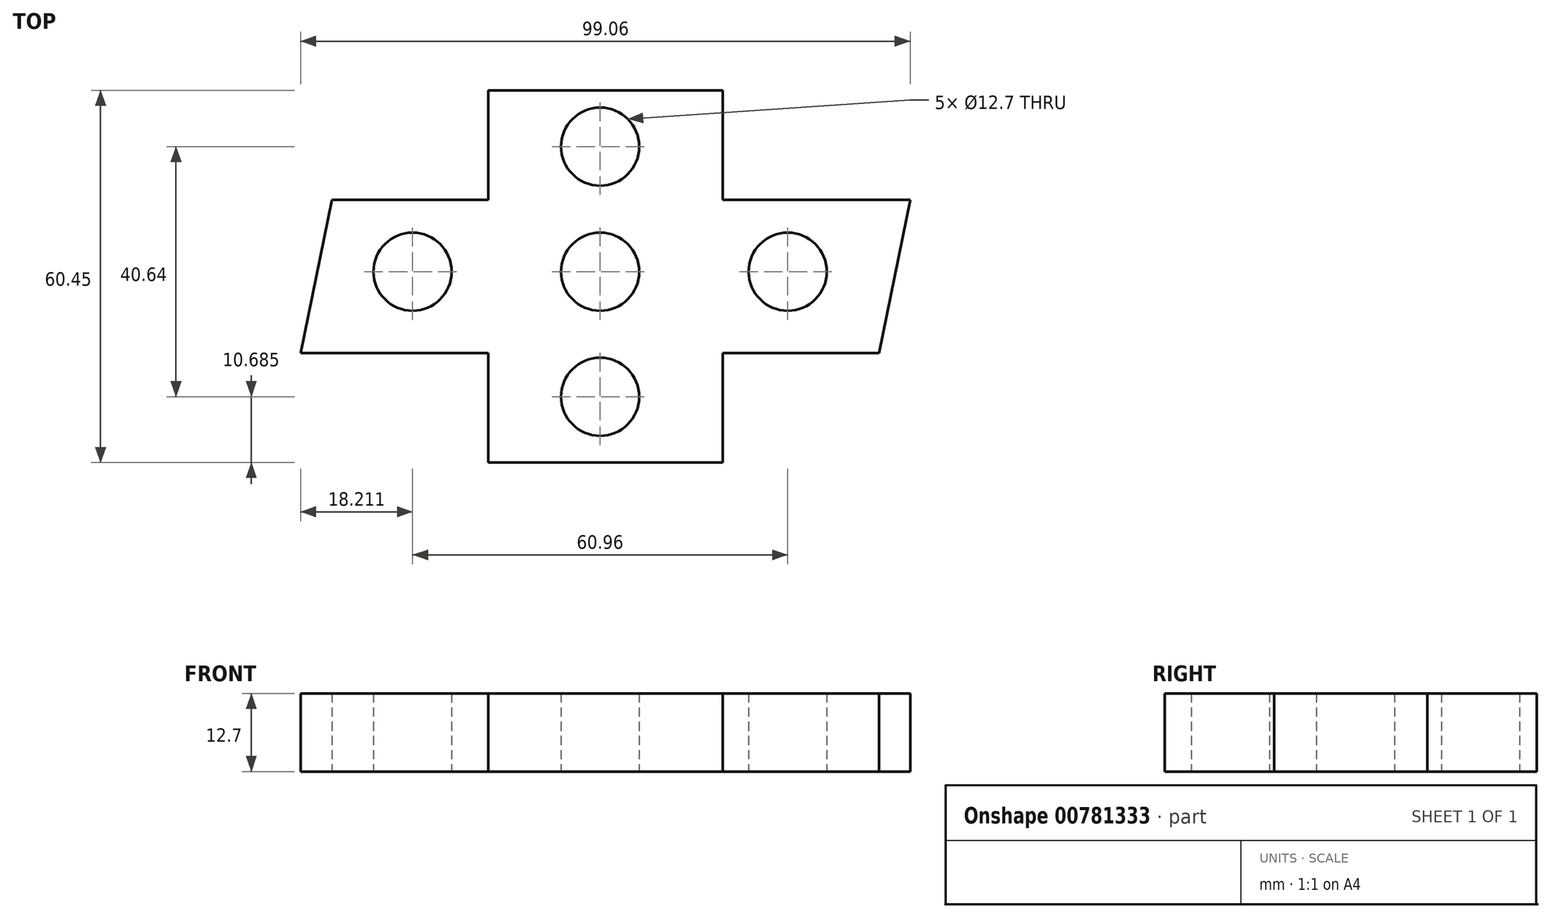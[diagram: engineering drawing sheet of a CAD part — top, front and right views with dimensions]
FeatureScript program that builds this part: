
annotation { "Feature Type Name" : "Feature", "Feature Type Description" : "" }
export const myFeature = defineFeature(function(context is Context, id is Id, definition is map)
    precondition{}
    {
        {
            var Q0;
            Q0=qCreatedBy(makeId("Top.planeOp"),FACE);
            var sketch = newSketch(context, id + "F0", { "sketchPlane" : qUnion([Q0])});
            skCircle(sketch, "E0", {"center": v(10.3, -62.12) * mm, "radius": 6.35 * mm});
            skCircle(sketch, "E1", {"center": v(10.3, -21.48) * mm, "radius": 6.35 * mm});
            skCircle(sketch, "E2", {"center": v(-20.19, -41.8) * mm, "radius": 6.35 * mm});
            skLineSegment(sketch, "E3", {"start": v(-7.92, -30.14) * mm, "end": v(-7.92, -12.36) * mm});
            skLineSegment(sketch, "E4", {"start": v(-7.92, -12.36) * mm, "end": v(30.18, -12.36) * mm});
            skLineSegment(sketch, "E5", {"start": v(30.18, -12.36) * mm, "end": v(30.18, -30.14) * mm});
            skLineSegment(sketch, "E6", {"start": v(30.18, -30.14) * mm, "end": v(60.66, -30.14) * mm});
            skLineSegment(sketch, "E7", {"start": v(60.66, -30.14) * mm, "end": v(55.58, -55.03) * mm});
            skLineSegment(sketch, "E8", {"start": v(55.58, -55.03) * mm, "end": v(30.18, -55.03) * mm});
            skLineSegment(sketch, "E9", {"start": v(30.18, -55.03) * mm, "end": v(30.18, -72.8) * mm});
            skLineSegment(sketch, "E10", {"start": v(30.18, -72.8) * mm, "end": v(-7.92, -72.8) * mm});
            skLineSegment(sketch, "E11", {"start": v(-7.92, -72.8) * mm, "end": v(-7.92, -55.03) * mm});
            skLineSegment(sketch, "E12", {"start": v(-7.92, -55.03) * mm, "end": v(-38.4, -55.03) * mm});
            skLineSegment(sketch, "E13", {"start": v(-38.4, -55.03) * mm, "end": v(-33.32, -30.14) * mm});
            skLineSegment(sketch, "E14", {"start": v(-33.32, -30.14) * mm, "end": v(-7.92, -30.14) * mm});
            skCircle(sketch, "E15", {"center": v(40.77, -41.8) * mm, "radius": 6.35 * mm});
            skCircle(sketch, "E16", {"center": v(10.3, -41.8) * mm, "radius": 6.35 * mm});
            skSolve(sketch);
        }
        {
            var Q0;
            Q0=makeQuery(id+"F0.imprint","IMPRINT",FACE,{"disambiguationData":[TD([[makeQuery(id+"F0.imprint","IMPRINT",EDGE,{"derivedFrom":sQuery(id+"F0.wireOp",EDGE,"E0")}),-1.0]])]});
            extrude(context, id + "F1", {"entities" : qUnion([Q0]), "depth" : 12.7 * mm, "offsetDistance" : 25.4 * mm});
        }
    });
